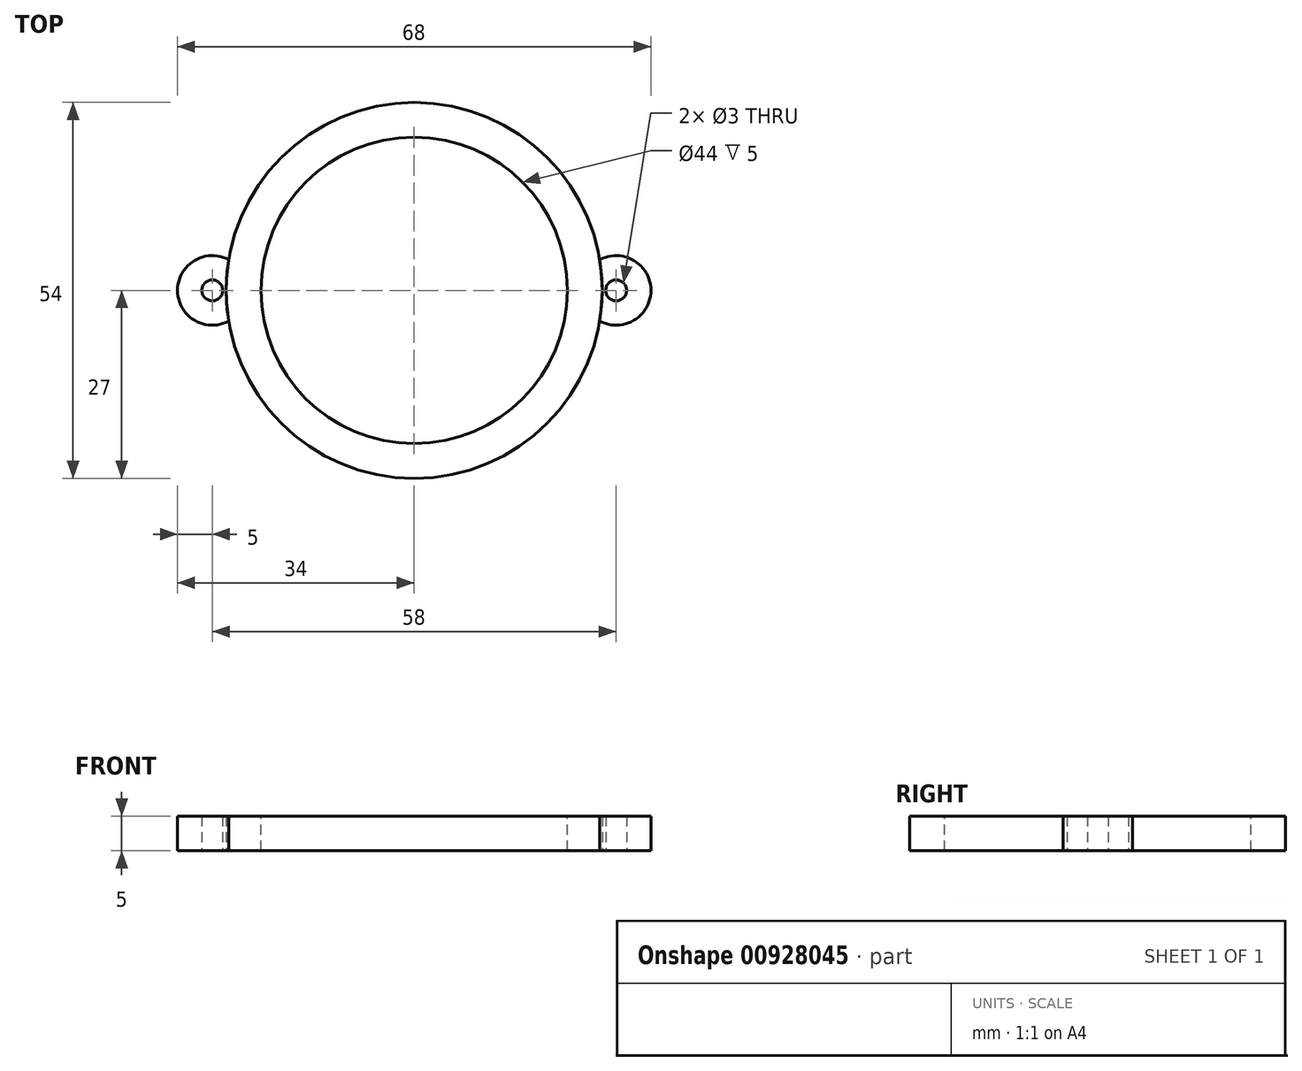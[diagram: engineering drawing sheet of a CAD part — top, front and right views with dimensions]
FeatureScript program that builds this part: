
annotation { "Feature Type Name" : "Feature", "Feature Type Description" : "" }
export const myFeature = defineFeature(function(context is Context, id is Id, definition is map)
    precondition{}
    {
        {
            var Q0;
            Q0=qCreatedBy(makeId("Top.planeOp"),FACE);
            var sketch = newSketch(context, id + "F0", { "sketchPlane" : qUnion([Q0])});
            skCircle(sketch, "E0", {"center": v(0, 0) * mm, "radius": 27 * mm});
            skCircle(sketch, "E1", {"center": v(29, 0) * mm, "radius": 5 * mm});
            skCircle(sketch, "E2", {"center": v(29, 0) * mm, "radius": 1.5 * mm});
            skCircle(sketch, "E3.1.0", {"center": v(-29, 0) * mm, "radius": 5 * mm});
            skCircle(sketch, "E3.1.1", {"center": v(-29, 0) * mm, "radius": 1.5 * mm});
            skSolve(sketch);
        }
        {
            var Q0;
            Q0=makeQuery(id+"F0.imprint","IMPRINT",FACE,{"disambiguationData":[TD([[makeQuery(id+"F0.imprint","IMPRINT",EDGE,{"derivedFrom":sQuery(id+"F0.wireOp",EDGE,"E3.1.1")}),-1.0]])]});
            var Q1;
            Q1=makeQuery(id+"F0.imprint","IMPRINT",FACE,{"disambiguationData":[TD([[makeQuery(id+"F0.imprint","IMPRINT",EDGE,{"derivedFrom":sQuery(id+"F0.wireOp",EDGE,"E2")}),-1.0]])]});
            extrude(context, id + "F1", {"entities" : qUnion([Q0, Q1]), "depth" : 5 * mm, "offsetDistance" : 25 * mm});
        }
        {
            var Q0;
            {var subQ0=sQuery(id+"F0.wireOp",EDGE,"E3.1.0");var subQ1=sQuery(id+"F0.wireOp",EDGE,"E0");var subQ2=makeQuery(id+"F0.imprint","INTERSECT",VERTEX,{"disambiguationData":[OD(0.0)],"derivedFrom":[subQ1,subQ0]});Q0=makeQuery(id+"F0.imprint","IMPRINT",FACE,{"disambiguationData":[TD([[makeQuery(id+"F0.imprint","IMPRINT",EDGE,{"disambiguationData":[TD([[subQ2,-1.0]])],"derivedFrom":subQ1}),1.0]])]});}
            var Q1;
            {var subQ0=sQuery(id+"F0.wireOp",EDGE,"E1");var subQ1=sQuery(id+"F0.wireOp",EDGE,"E0");var subQ2=makeQuery(id+"F0.imprint","INTERSECT",VERTEX,{"disambiguationData":[OD(0.0)],"derivedFrom":[subQ1,subQ0]});Q1=makeQuery(id+"F0.imprint","IMPRINT",FACE,{"disambiguationData":[TD([[makeQuery(id+"F0.imprint","IMPRINT",EDGE,{"disambiguationData":[TD([[subQ2,1.0]])],"derivedFrom":subQ1}),1.0]])]});}
            var Q2;
            {var subQ0=sQuery(id+"F0.wireOp",EDGE,"E3.1.0");var subQ1=sQuery(id+"F0.wireOp",EDGE,"E0");var subQ2=makeQuery(id+"F0.imprint","INTERSECT",VERTEX,{"disambiguationData":[OD(0.0)],"derivedFrom":[subQ1,subQ0]});Q2=makeQuery(id+"F0.imprint","IMPRINT",FACE,{"disambiguationData":[TD([[makeQuery(id+"F0.imprint","IMPRINT",EDGE,{"disambiguationData":[TD([[subQ2,1.0]])],"derivedFrom":subQ1}),1.0]])]});}
            extrude(context, id + "F2", {"entities" : qUnion([Q0, Q1, Q2]), "depth" : 5 * mm, "offsetDistance" : 25 * mm});
        }
        {
            var Q0;
            Q0=makeQuery(id+"F2.opExtrude","CAP_FACE",FACE,{"disambiguationData":[OSD([sQuery(id+"F0.wireOp",EDGE,"E0")])],"isStart":false});
            var sketch = newSketch(context, id + "F3", { "sketchPlane" : qUnion([Q0])});
            skCircle(sketch, "E4", {"center": v(0, 0) * mm, "radius": 22 * mm});
            skSolve(sketch);
        }
        {
            var Q0;
            Q0=makeQuery(id+"F3.imprint","IMPRINT",FACE,{"disambiguationData":[TD([[makeQuery(id+"F3.imprint","IMPRINT",EDGE,{"derivedFrom":sQuery(id+"F3.wireOp",EDGE,"E4")}),1.0]])]});
            extrude(context, id + "F4", {"entities" : qUnion([Q0]), "operationType" : NewBodyOperationType.REMOVE, "oppositeDirection" : true, "depth" : 6 * mm, "offsetDistance" : 25 * mm});
        }
    });
